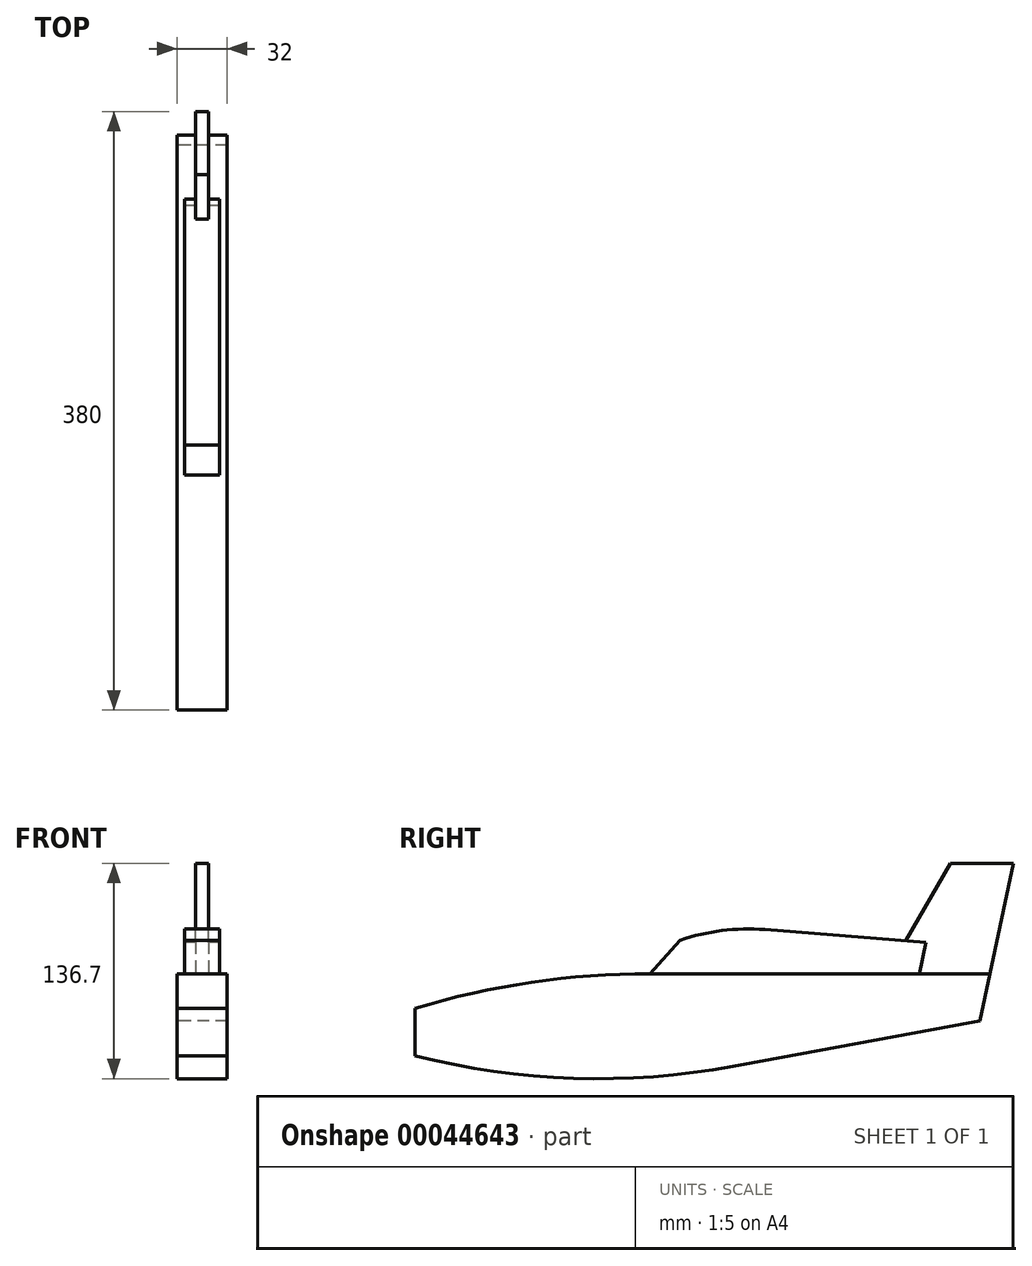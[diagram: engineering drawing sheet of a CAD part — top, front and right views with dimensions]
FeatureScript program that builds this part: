
annotation { "Feature Type Name" : "Feature", "Feature Type Description" : "" }
export const myFeature = defineFeature(function(context is Context, id is Id, definition is map)
    precondition{}
    {
        {
            var Q0;
            Q0=qCreatedBy(makeId("Right.planeOp"),FACE);
            var sketch = newSketch(context, id + "F0", { "sketchPlane" : qUnion([Q0])});
            skLineSegment(sketch, "E0", {"start": v(-159.2, 0) * mm, "end": v(163.88, 0) * mm, "construction": true});
            skSolve(sketch);
        }
        {
            var Q0;
            Q0=qCreatedBy(makeId("Right.planeOp"),FACE);
            var sketch = newSketch(context, id + "F1", { "sketchPlane" : qUnion([Q0])});
            skArc(sketch, "E1", {"start": v(0, 25) * mm, "mid": v(-75.43, 19.45) * mm, "end": v(-149.23, 2.93) * mm});
            skLineSegment(sketch, "E2", {"start": v(-149.23, 2.93) * mm, "end": v(-149.23, 0) * mm});
            skLineSegment(sketch, "E3", {"start": v(0, 25) * mm, "end": v(215.9, 25) * mm});
            skLineSegment(sketch, "E4", {"start": v(150.36, 25) * mm, "end": v(190.77, 95) * mm});
            skLineSegment(sketch, "E5", {"start": v(190.77, 95) * mm, "end": v(230.77, 95) * mm});
            skLineSegment(sketch, "E6", {"start": v(230.77, 95) * mm, "end": v(209.51, -5) * mm});
            skLineSegment(sketch, "E7", {"start": v(-149.23, 0) * mm, "end": v(-149.23, -27.07) * mm});
            skLineSegment(sketch, "E8", {"start": v(209.51, -5) * mm, "end": v(52.67, -33.9) * mm});
            skArc(sketch, "E9", {"start": v(-149.23, -27.07) * mm, "mid": v(-48.65, -41.43) * mm, "end": v(52.67, -33.9) * mm});
            skLineSegment(sketch, "E10", {"start": v(175.34, 45) * mm, "end": v(72.86, 53) * mm});
            skPoint(sketch, "E10.startSnap0", {"position": v(220.14, 45) * mm});
            skLineSegment(sketch, "E11", {"start": v(175.34, 45) * mm, "end": v(171.1, 25) * mm});
            skLineSegment(sketch, "E12", {"start": v(0, 25) * mm, "end": v(19.11, 46.23) * mm});
            skArc(sketch, "E13", {"start": v(72.86, 53) * mm, "mid": v(45.64, 52.35) * mm, "end": v(19.11, 46.23) * mm});
            skSolve(sketch);
        }
        {
            var Q0;
            {var subQ3=sQuery(id+"F1.wireOp",EDGE,"E1");Q0=makeQuery(id+"F1.imprint","IMPRINT",FACE,{"disambiguationData":[TD([[makeQuery(id+"F1.imprint","IMPRINT",EDGE,{"derivedFrom":subQ3}),1.0]])]});}
            extrude(context, id + "F2", {"entities" : qUnion([Q0]), "depth" : 32 * mm, "symmetric" : true});
        }
        {
            var Q0;
            {var subQ3=sQuery(id+"F1.wireOp",EDGE,"E5");Q0=makeQuery(id+"F1.imprint","IMPRINT",FACE,{"disambiguationData":[TD([[makeQuery(id+"F1.imprint","IMPRINT",EDGE,{"derivedFrom":subQ3}),-1.0]])]});}
            extrude(context, id + "F3", {"entities" : qUnion([Q0]), "operationType" : NewBodyOperationType.ADD, "depth" : 8 * mm, "symmetric" : true});
        }
        {
            var Q0;
            {var subQ3=sQuery(id+"F1.wireOp",EDGE,"E11");Q0=makeQuery(id+"F1.imprint","IMPRINT",FACE,{"disambiguationData":[TD([[makeQuery(id+"F1.imprint","IMPRINT",EDGE,{"derivedFrom":subQ3}),-1.0]])]});}
            var Q1;
            {var subQ4=sQuery(id+"F1.wireOp",EDGE,"E12");Q1=makeQuery(id+"F1.imprint","IMPRINT",FACE,{"disambiguationData":[TD([[makeQuery(id+"F1.imprint","IMPRINT",EDGE,{"derivedFrom":subQ4}),-1.0]])]});}
            extrude(context, id + "F4", {"entities" : qUnion([Q0, Q1]), "operationType" : NewBodyOperationType.ADD, "depth" : 22 * mm, "symmetric" : true});
        }
    });
